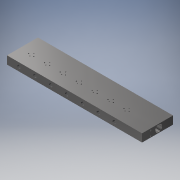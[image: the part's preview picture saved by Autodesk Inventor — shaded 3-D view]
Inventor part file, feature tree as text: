
AUTODESK INVENTOR PART (.ipt)
format: ipt  version: 2018 (Build 220112000, 112)  size: 281,088 bytes
history: native  units: mm
features: hole x8, pattern_linear x2, sketch x2, extrude x1
ambient origin geometry x8: Origin, YZ Plane, XZ Plane, XY Plane, X Axis, Y Axis, Z Axis, Center Point
bodies: Volumenkörper1 (feature_tree)
feature tree (13):
  extrude  "Extrusion1"  Depth=170.0mm
  hole  "Bohrung1"  [1 undecoded]
  hole  "Bohrung2"  [1 undecoded]
  pattern_linear  "Rechteckige Anordnung1"  Spacing1=5.0mm  [1 undecoded]
  hole  "Bohrung5"  [1 undecoded]
  hole  "Bohrung6"  [1 undecoded]
  pattern_linear  "Rechteckige Anordnung2"  Spacing1=2.0mm  [1 undecoded]
  hole  "Bohrung14"  [1 undecoded]
  hole  "Bohrung15"  [1 undecoded]
  hole  "Bohrung16"  [1 undecoded]
  hole  "Bohrung17"  [1 undecoded]
  sketch  "Skizze2"  dims[d0=39.0mm d1=170.0mm]
  sketch  "Skizze10"  dims[d2=10.0mm d3=0.0mm d6=10.0mm d7=27.0mm d8=5.0mm d9=10.0mm d10=3.8mm d11=2.0mm d12=5.0mm d13=1.2mm d14=6.0mm d15=4.0mm d16=2.0mm d17=90.0deg d18=5.0mm d19=20.594885mm d20=3.25mm d21=3.25mm d22=1.7mm d23=1.7mm d24=1.221mm d25=5.0mm d26=4.0mm d27=2.0mm d28=90.0deg d29=7.0mm d30=20.594885mm d41=70.0mm d43=20.0mm d53=15.0mm d54=5.0mm d55=2.0mm d56=6.0mm d57=4.0mm d58=2.0mm d59=90.0deg d60=14.0mm d61=20.594885mm d73=10.0mm d74=10.0mm d64=4.134mm d65=6.0mm d66=4.0mm d67=2.0mm d68=90.0deg d69=7.0mm d70=20.594885mm d71=70.0mm d75=20.0mm d145=28.0mm d146=28.0mm d147=2.0mm d148=2.0mm d149=2.459mm d150=10.0mm d151=4.0mm d152=2.0mm d153=90.0deg d154=12.0mm d155=20.594885mm d156=2.459mm d157=10.0mm d158=4.0mm d159=2.0mm d160=90.0deg d161=12.0mm d162=20.594885mm d163=18.0mm d164=8.0mm d165=8.0mm d166=10.0mm d167=4.0mm d168=2.0mm d169=90.0deg d170=166.0mm d171=135.0deg d172=10.0mm d173=10.0mm d174=8.6mm d175=10.0mm d176=4.0mm d177=2.0mm d178=90.0deg d179=12.0mm d180=135.0deg]
note: 10 required parameter values undecoded (feature->parameter linkage not recoverable at this tier; creation-order binding heuristic only, values carry confidence <= 0.55)
